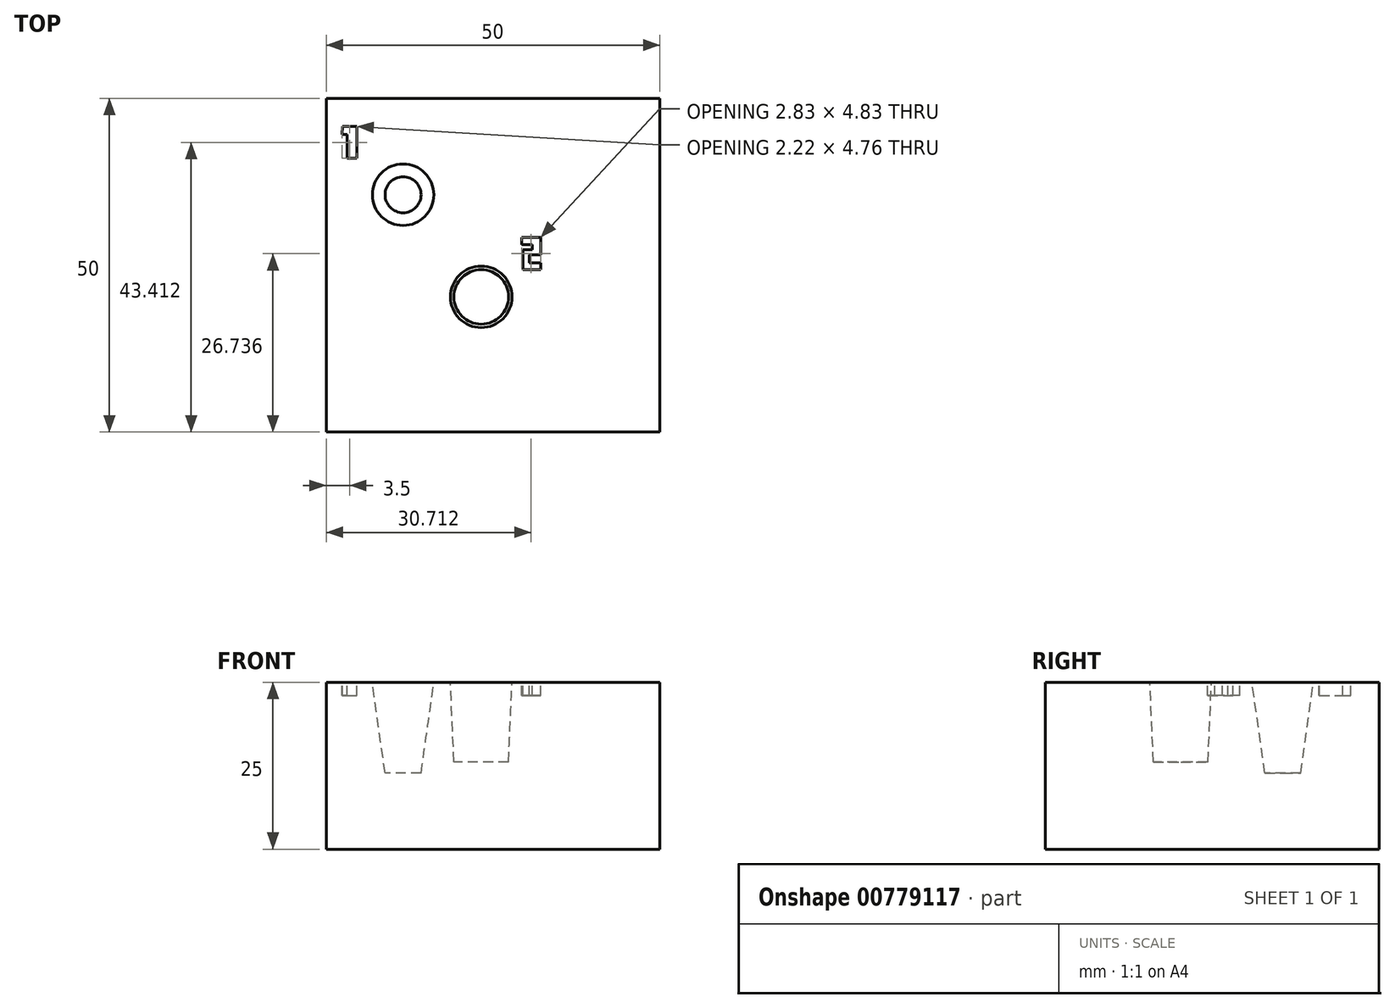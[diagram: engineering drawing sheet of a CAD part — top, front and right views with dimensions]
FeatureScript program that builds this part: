
annotation { "Feature Type Name" : "Feature", "Feature Type Description" : "" }
export const myFeature = defineFeature(function(context is Context, id is Id, definition is map)
    precondition{}
    {
        {
            var Q0;
            Q0=qCreatedBy(makeId("Front.planeOp"),FACE);
            var sketch = newSketch(context, id + "F0", { "sketchPlane" : qUnion([Q0])});
            skLineSegment(sketch, "E0.bottom", {"start": v(-23.23, 12.9) * mm, "end": v(26.77, 12.9) * mm});
            skLineSegment(sketch, "E0.top", {"start": v(-23.23, -12.1) * mm, "end": v(26.77, -12.1) * mm});
            skLineSegment(sketch, "E0.left", {"start": v(-23.23, 12.9) * mm, "end": v(-23.23, -12.1) * mm});
            skLineSegment(sketch, "E0.right", {"start": v(26.77, 12.9) * mm, "end": v(26.77, -12.1) * mm});
            skSolve(sketch);
        }
        {
            var Q0;
            Q0=makeQuery(id+"F0.imprint","IMPRINT",FACE,{"disambiguationData":[TD([[makeQuery(id+"F0.imprint","IMPRINT",EDGE,{"derivedFrom":sQuery(id+"F0.wireOp",EDGE,"E0.bottom")}),-1.0]])]});
            extrude(context, id + "F1", {"entities" : qUnion([Q0]), "depth" : 50 * mm, "offsetDistance" : 25 * mm});
        }
        {
            var Q0;
            Q0=makeQuery(id+"F1.opExtrude","SWEPT_FACE",FACE,{"disambiguationData":[OSD([sQuery(id+"F0.wireOp",EDGE,"E0.bottom")])]});
            var sketch = newSketch(context, id + "F2", { "sketchPlane" : qUnion([Q0])});
            skCircle(sketch, "E1", {"center": v(0, -29.73) * mm, "radius": 4.61 * mm});
            skSolve(sketch);
        }
        {
            var Q0;
            Q0=makeQuery(id+"F2.imprint","IMPRINT",FACE,{"disambiguationData":[TD([[makeQuery(id+"F2.imprint","IMPRINT",EDGE,{"derivedFrom":sQuery(id+"F2.wireOp",EDGE,"E1")}),1.0]])]});
            var Q1;
            Q1=sQuery(id+"F2.wireOp",EDGE,"E1");
            extrude(context, id + "F3", {"entities" : qUnion([Q0]), "operationType" : NewBodyOperationType.REMOVE, "surfaceEntities" : qUnion([Q1]), "oppositeDirection" : true, "depth" : 11.94 * mm, "offsetDistance" : 25 * mm, "hasDraft" : true, "draftAngle" : 2.5 * degree, "draftPullDirection" : true});
        }
        {
            var Q0;
            Q0=makeQuery(id+"F1.opExtrude","SWEPT_FACE",FACE,{"disambiguationData":[OSD([sQuery(id+"F0.wireOp",EDGE,"E0.bottom")])]});
            var sketch = newSketch(context, id + "F4", { "sketchPlane" : qUnion([Q0])});
            skCircle(sketch, "E2", {"center": v(-11.71, -14.43) * mm, "radius": 4.61 * mm});
            skSolve(sketch);
        }
        {
            var Q0;
            Q0=makeQuery(id+"F4.imprint","IMPRINT",FACE,{"disambiguationData":[TD([[makeQuery(id+"F4.imprint","IMPRINT",EDGE,{"derivedFrom":sQuery(id+"F4.wireOp",EDGE,"E2")}),1.0]])]});
            extrude(context, id + "F5", {"entities" : qUnion([Q0]), "operationType" : NewBodyOperationType.REMOVE, "oppositeDirection" : true, "depth" : 13.6 * mm, "offsetDistance" : 25 * mm, "hasDraft" : true, "draftAngle" : 8 * degree, "draftPullDirection" : true});
        }
        {
            var Q0;
            Q0=makeQuery(id+"F1.opExtrude","SWEPT_FACE",FACE,{"disambiguationData":[OSD([sQuery(id+"F0.wireOp",EDGE,"E0.bottom")])]});
            var sketch = newSketch(context, id + "F6", { "sketchPlane" : qUnion([Q0])});
            skLineSegment(sketch, "E3", {"start": v(-20.12, -8.97) * mm, "end": v(-20.12, -5.43) * mm});
            skLineSegment(sketch, "E4", {"start": v(-20.12, -5.43) * mm, "end": v(-20.84, -5.43) * mm});
            skLineSegment(sketch, "E5", {"start": v(-20.84, -5.43) * mm, "end": v(-20.81, -4.2) * mm});
            skLineSegment(sketch, "E6", {"start": v(-20.81, -4.2) * mm, "end": v(-18.62, -4.2) * mm});
            skLineSegment(sketch, "E7", {"start": v(-18.62, -4.2) * mm, "end": v(-18.62, -5.43) * mm});
            skLineSegment(sketch, "E8", {"start": v(-18.62, -8.92) * mm, "end": v(-18.62, -5.43) * mm});
            skLineSegment(sketch, "E9", {"start": v(-20.12, -8.97) * mm, "end": v(-18.62, -8.92) * mm});
            skLineSegment(sketch, "E10", {"start": v(8.9, -21.9) * mm, "end": v(8.9, -23.46) * mm});
            skLineSegment(sketch, "E11", {"start": v(8.9, -23.46) * mm, "end": v(7.23, -23.46) * mm});
            skLineSegment(sketch, "E12", {"start": v(7.23, -23.46) * mm, "end": v(7.23, -24.62) * mm});
            skLineSegment(sketch, "E13", {"start": v(7.23, -24.62) * mm, "end": v(8.9, -24.62) * mm});
            skLineSegment(sketch, "E14", {"start": v(8.9, -24.62) * mm, "end": v(8.9, -25.68) * mm});
            skLineSegment(sketch, "E15", {"start": v(8.9, -25.68) * mm, "end": v(6.23, -25.68) * mm});
            skLineSegment(sketch, "E16", {"start": v(6.23, -25.68) * mm, "end": v(6.23, -22.68) * mm});
            skLineSegment(sketch, "E17", {"start": v(6.23, -22.68) * mm, "end": v(7.68, -22.68) * mm});
            skLineSegment(sketch, "E18", {"start": v(7.68, -22.68) * mm, "end": v(7.68, -21.9) * mm});
            skLineSegment(sketch, "E19", {"start": v(7.68, -21.9) * mm, "end": v(6.07, -21.9) * mm});
            skLineSegment(sketch, "E20", {"start": v(6.07, -20.85) * mm, "end": v(8.9, -20.85) * mm});
            skLineSegment(sketch, "E21", {"start": v(8.9, -20.85) * mm, "end": v(8.9, -21.9) * mm});
            skLineSegment(sketch, "E22", {"start": v(6.07, -20.85) * mm, "end": v(6.07, -21.9) * mm});
            skSolve(sketch);
        }
        {
            var Q0;
            Q0 = qSketchRegion(id + "F6", true);
            extrude(context, id + "F7", {"entities" : qUnion([Q0]), "operationType" : NewBodyOperationType.REMOVE, "oppositeDirection" : true, "depth" : 2 * mm, "offsetDistance" : 25 * mm});
        }
    });
